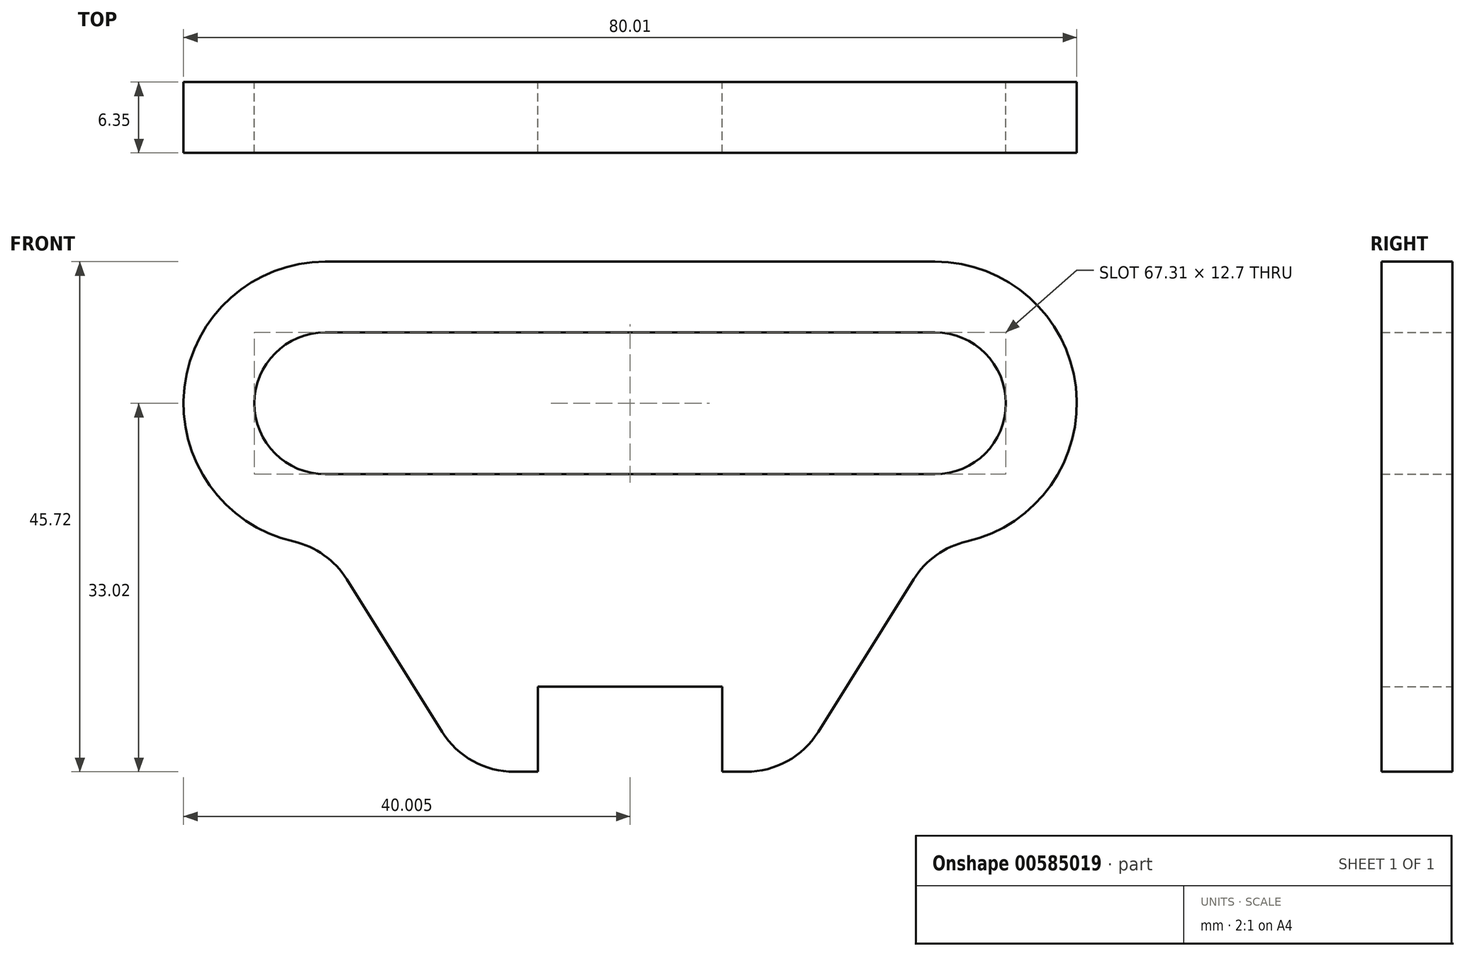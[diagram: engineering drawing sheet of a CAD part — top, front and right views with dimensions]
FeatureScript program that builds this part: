
annotation { "Feature Type Name" : "Feature", "Feature Type Description" : "" }
export const myFeature = defineFeature(function(context is Context, id is Id, definition is map)
    precondition{}
    {
        {
            var Q0;
            Q0=qCreatedBy(makeId("Front.planeOp"),FACE);
            var sketch = newSketch(context, id + "F0", { "sketchPlane" : qUnion([Q0])});
            skLineSegment(sketch, "E0", {"start": v(0, 0) * mm, "end": v(0, 7.62) * mm});
            skLineSegment(sketch, "E1", {"start": v(0, 7.62) * mm, "end": v(16.51, 7.62) * mm});
            skLineSegment(sketch, "E2", {"start": v(16.51, 7.62) * mm, "end": v(16.51, 0) * mm});
            skArc(sketch, "E3", {"start": v(35.56, 20.32) * mm, "mid": v(48.26, 33.02) * mm, "end": v(35.56, 45.72) * mm});
            skArc(sketch, "E4", {"start": v(-19.05, 45.72) * mm, "mid": v(-31.75, 33.02) * mm, "end": v(-19.05, 20.32) * mm});
            skLineSegment(sketch, "E5", {"start": v(-19.05, 33.02) * mm, "end": v(35.56, 33.02) * mm, "construction": true});
            skLineSegment(sketch, "E6", {"start": v(-19.05, 33.02) * mm, "end": v(-19.05, 20.32) * mm, "construction": true});
            skLineSegment(sketch, "E7", {"start": v(35.56, 33.02) * mm, "end": v(35.56, 20.32) * mm, "construction": true});
            skLineSegment(sketch, "E8", {"start": v(-19.05, 45.72) * mm, "end": v(35.56, 45.72) * mm});
            skLineSegment(sketch, "E9", {"start": v(16.51, 0) * mm, "end": v(22.86, 0) * mm});
            skLineSegment(sketch, "E10", {"start": v(22.86, 0) * mm, "end": v(35.56, 20.32) * mm});
            skLineSegment(sketch, "E11", {"start": v(0, 0) * mm, "end": v(-6.35, 0) * mm});
            skLineSegment(sketch, "E12", {"start": v(-6.35, 0) * mm, "end": v(-19.05, 20.32) * mm});
            skArc(sketch, "E13.0.startCap", {"start": v(-19.05, 26.67) * mm, "mid": v(-25.4, 33.02) * mm, "end": v(-19.05, 39.37) * mm});
            skArc(sketch, "E13.0.endCap", {"start": v(35.56, 39.37) * mm, "mid": v(41.91, 33.02) * mm, "end": v(35.56, 26.67) * mm});
            skLineSegment(sketch, "E13.0.left", {"start": v(-19.05, 39.37) * mm, "end": v(35.56, 39.37) * mm});
            skLineSegment(sketch, "E13.0.right", {"start": v(-19.05, 26.67) * mm, "end": v(35.56, 26.67) * mm});
            skSolve(sketch);
        }
        {
            var Q0;
            Q0 = qSketchRegion(id + "F0", true);
            extrude(context, id + "F1", {"entities" : qUnion([Q0]), "depth" : 6.35 * mm, "offsetDistance" : 25.4 * mm});
        }
        {
            var Q0;
            Q0=makeQuery(id+"F1.opExtrude","SWEPT_EDGE",EDGE,{"disambiguationData":[OSD([sQuery(id+"F0.wireOp",EDGE,"E9"),sQuery(id+"F0.wireOp",EDGE,"E10")])]});
            var Q1;
            Q1=makeQuery(id+"F1.opExtrude","SWEPT_EDGE",EDGE,{"disambiguationData":[OSD([sQuery(id+"F0.wireOp",EDGE,"E11"),sQuery(id+"F0.wireOp",EDGE,"E12")])]});
            var Q2;
            Q2=makeQuery(id+"F1.opExtrude","SWEPT_EDGE",EDGE,{"disambiguationData":[OSD([sQuery(id+"F0.wireOp",EDGE,"E3"),sQuery(id+"F0.wireOp",EDGE,"E10")])]});
            var Q3;
            Q3=makeQuery(id+"F1.opExtrude","SWEPT_EDGE",EDGE,{"disambiguationData":[OSD([sQuery(id+"F0.wireOp",EDGE,"E4"),sQuery(id+"F0.wireOp",EDGE,"E12")])]});
            fillet(context, id + "F2", {"entities" : qUnion([Q0, Q1, Q2, Q3]), "tangentPropagation" : true, "radius" : 7.62 * mm, "defaultsChanged" : true, "vertexSettings" : [], "allowEdgeOverflow" : false});
        }
    });
